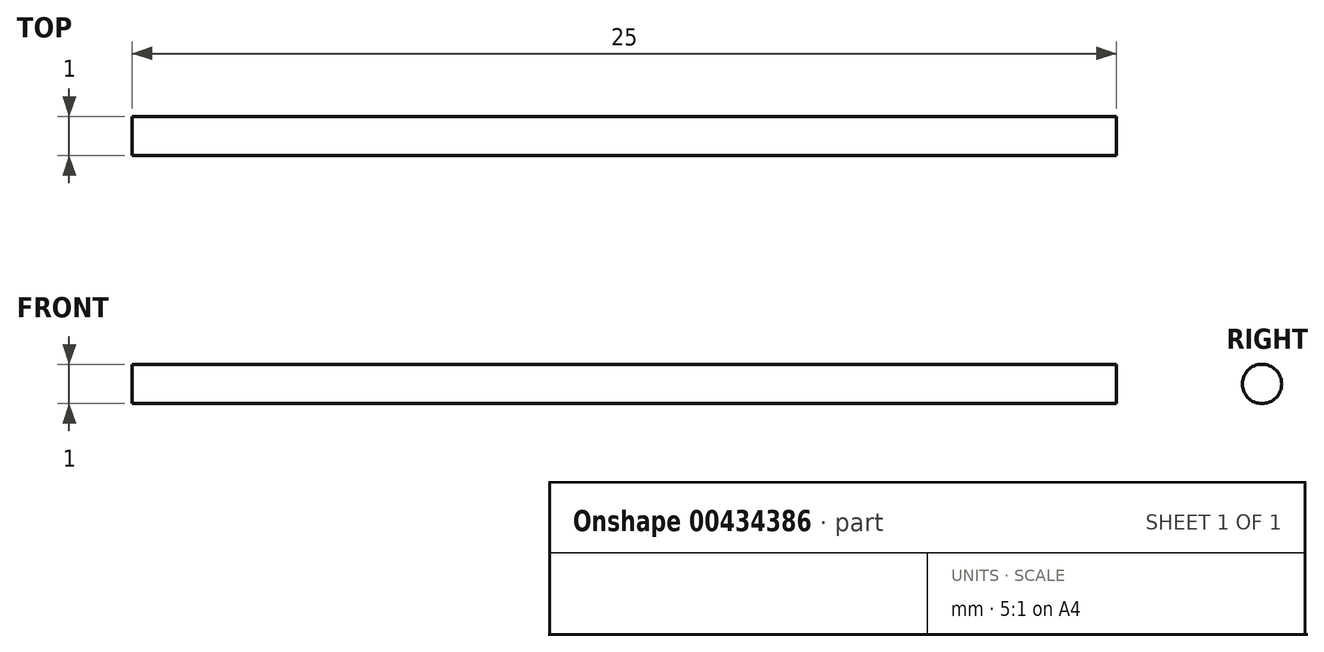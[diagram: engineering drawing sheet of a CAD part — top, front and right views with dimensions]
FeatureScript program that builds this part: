
annotation { "Feature Type Name" : "Feature", "Feature Type Description" : "" }
export const myFeature = defineFeature(function(context is Context, id is Id, definition is map)
    precondition{}
    {
        {
            var Q0;
            Q0=qCreatedBy(makeId("Right.planeOp"),FACE);
            var sketch = newSketch(context, id + "F0", { "sketchPlane" : qUnion([Q0])});
            skCircle(sketch, "E0", {"center": v(0, 0) * mm, "radius": 0.5 * mm});
            skSolve(sketch);
        }
        {
            var Q0;
            Q0 = qSketchRegion(id + "F0", true);
            extrude(context, id + "F1", {"entities" : qUnion([Q0]), "depth" : 25 * mm});
        }
    });
